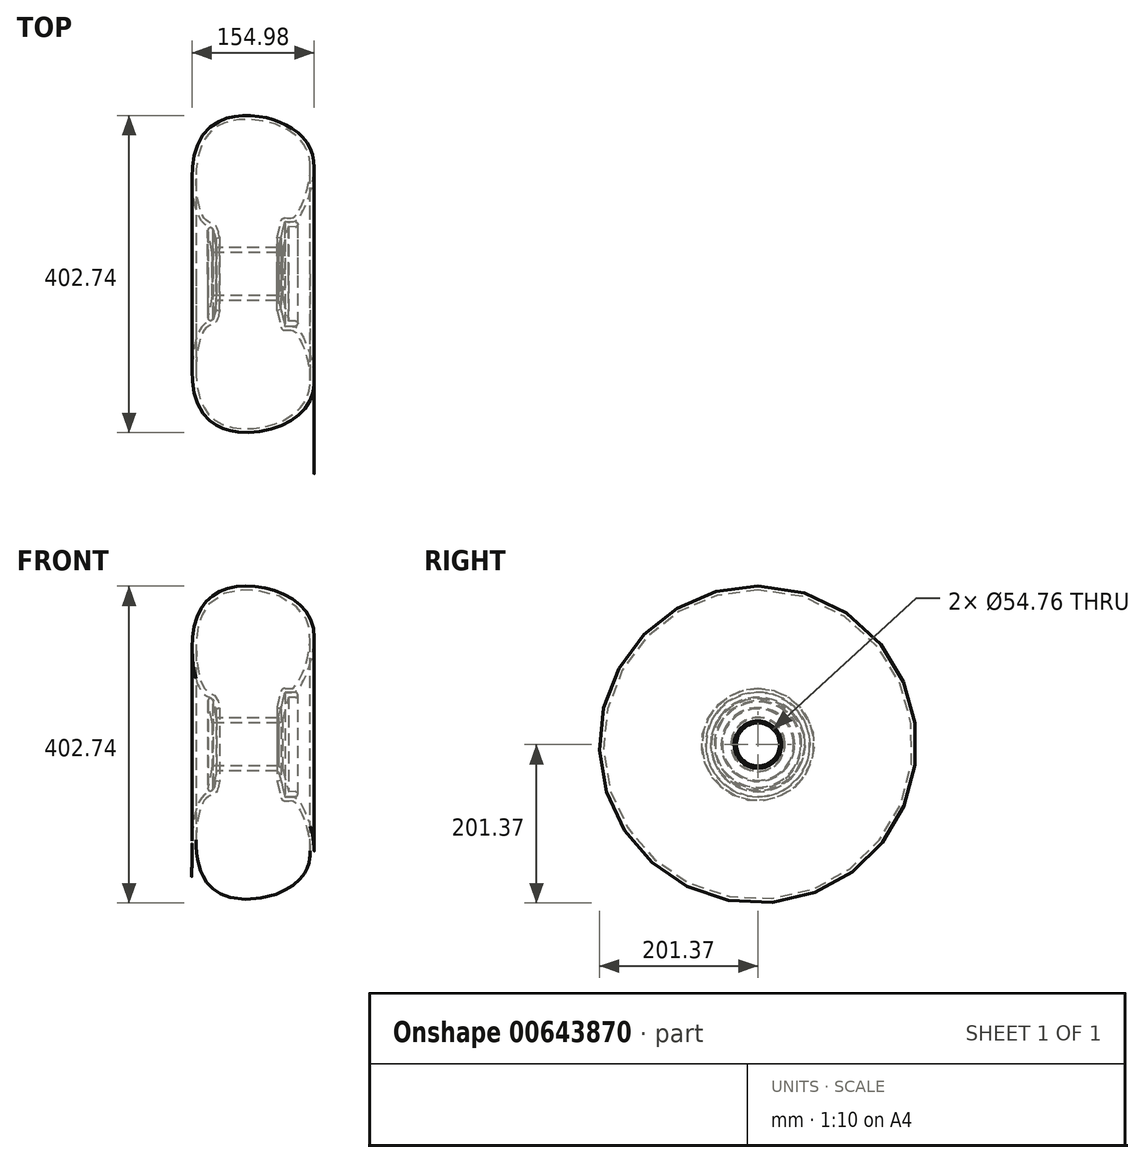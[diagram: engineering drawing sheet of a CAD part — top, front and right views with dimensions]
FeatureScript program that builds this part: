
annotation { "Feature Type Name" : "Feature", "Feature Type Description" : "" }
export const myFeature = defineFeature(function(context is Context, id is Id, definition is map)
    precondition{}
    {
        {
            var Q0;
            Q0=qCreatedBy(makeId("Front.planeOp"),FACE);
            var sketch = newSketch(context, id + "F0", { "sketchPlane" : qUnion([Q0])});
            skLineSegment(sketch, "E0", {"start": v(-28.23, 33.73) * mm, "end": v(49.08, 33.73) * mm});
            skLineSegment(sketch, "E1", {"start": v(50.61, 34.5) * mm, "end": v(49.08, 33.73) * mm});
            skLineSegment(sketch, "E2", {"start": v(49.08, 33.73) * mm, "end": v(50.61, 34.5) * mm});
            skLineSegment(sketch, "E3", {"start": v(58.9, 66.45) * mm, "end": v(50.61, 34.5) * mm});
            skLineSegment(sketch, "E4", {"start": v(72.2, 66.15) * mm, "end": v(58.9, 66.45) * mm});
            skLineSegment(sketch, "E5", {"start": v(-32.55, 55.46) * mm, "end": v(-28.23, 33.73) * mm});
            skLineSegment(sketch, "E6.0", {"start": v(72.05, 59.8) * mm, "end": v(63.79, 59.99) * mm});
            skLineSegment(sketch, "E6.1", {"start": v(-38.78, 54.22) * mm, "end": v(-33.44, 27.38) * mm});
            skLineSegment(sketch, "E6.2", {"start": v(-33.44, 27.38) * mm, "end": v(50.6, 27.38) * mm});
            skLineSegment(sketch, "E6.3", {"start": v(56.04, 30.14) * mm, "end": v(50.6, 27.38) * mm});
            skLineSegment(sketch, "E6.4", {"start": v(63.79, 59.99) * mm, "end": v(56.04, 30.14) * mm});
            skArc(sketch, "E7", {"start": v(72.05, 59.8) * mm, "mid": v(75.3, 62.9) * mm, "end": v(72.2, 66.15) * mm});
            skArc(sketch, "E8", {"start": v(-32.55, 55.46) * mm, "mid": v(-36.46, 58.82) * mm, "end": v(-38.78, 54.22) * mm});
            skLineSegment(sketch, "E9", {"start": v(0, 0) * mm, "end": v(20.87, 0) * mm, "construction": true});
            skSolve(sketch);
        }
        {
            var Q0;
            Q0 = qSketchRegion(id + "F0", true);
            var Q1;
            Q1=sQuery(id+"F0.wireOp",EDGE,"E9");
            revolve(context, id + "F1", {"entities" : qUnion([Q0]), "axis" : qUnion([Q1]), "revolveType" : RevolveType.FULL});
        }
        {
            var Q0;
            Q0=qCreatedBy(makeId("Front.planeOp"),FACE);
            var sketch = newSketch(context, id + "F2", { "sketchPlane" : qUnion([Q0])});
            skLineSegment(sketch, "E10", {"start": v(53.97, 45.4) * mm, "end": v(58.9, 66.45) * mm});
            skLineSegment(sketch, "E11", {"start": v(50.61, 34.5) * mm, "end": v(58.9, 66.45) * mm});
            skFitSpline(sketch, "E12", {"points": [v(58.9, 66.45) * mm, v(76.88, 71.82) * mm, v(93.15, 154.6) * mm, v(13.57, 201.31) * mm, v(-52.17, 164.12) * mm, v(-46.36, 66.45) * mm, v(-32.61, 57.36) * mm, v(-28.88, 45.27) * mm], "startDerivative": vector(355.83, -13.94) * mm, "endDerivative": vector(60.8, -192.56) * mm});
            skFitSpline(sketch, "E13.0", {"points": [v(59.1, 71.44) * mm, v(60.96, 71.37) * mm, v(63.36, 71.27) * mm, v(65.83, 71.25) * mm, v(67.31, 71.31) * mm, v(68.44, 71.45) * mm, v(69.25, 71.64) * mm, v(69.84, 71.86) * mm, v(70.36, 72.15) * mm, v(70.95, 72.6) * mm, v(71.7, 73.33) * mm, v(72.6, 74.42) * mm, v(73.65, 75.89) * mm, v(74.8, 77.68) * mm, v(76.44, 80.47) * mm, v(78.6, 84.62) * mm, v(81.23, 90.5) * mm, v(83.76, 97.08) * mm, v(86.1, 104.22) * mm, v(88.1, 111.74) * mm, v(89.66, 119.5) * mm, v(90.69, 127.34) * mm, v(91.07, 135.07) * mm, v(90.77, 141.3) * mm, v(90.12, 146.07) * mm, v(89.43, 149.52) * mm, v(88.66, 152.28) * mm, v(87.94, 154.4) * mm, v(86.73, 157.55) * mm, v(84.49, 162.04) * mm, v(80.63, 167.58) * mm, v(75.98, 172.69) * mm, v(68.83, 178.9) * mm, v(58.3, 185.47) * mm, v(43.91, 191.33) * mm, v(31.17, 194.46) * mm, v(20.96, 195.88) * mm, v(13.4, 196.4) * mm, v(6.04, 196.39) * mm, v(-3.4, 195.62) * mm, v(-14.44, 193.27) * mm, v(-26.12, 188.15) * mm, v(-34.36, 181.92) * mm, v(-39.98, 175.67) * mm, v(-43.07, 171.2) * mm, v(-45.27, 167.26) * mm, v(-46.78, 164.12) * mm, v(-48.14, 160.8) * mm, v(-49.36, 157.26) * mm, v(-50.43, 153.55) * mm, v(-51.67, 148.39) * mm, v(-52.87, 141.6) * mm, v(-53.75, 133.08) * mm, v(-54.23, 121.48) * mm, v(-53.72, 109.87) * mm, v(-52.37, 98.94) * mm, v(-50.96, 91.26) * mm, v(-49.22, 84.3) * mm, v(-47.54, 79.24) * mm, v(-46.09, 75.75) * mm, v(-44.97, 73.43) * mm, v(-43.83, 71.46) * mm, v(-42.9, 70.12) * mm, v(-42.19, 69.24) * mm, v(-41.48, 68.46) * mm, v(-40.58, 67.64) * mm, v(-39.5, 66.83) * mm, v(-38.36, 66.14) * mm, v(-37.18, 65.53) * mm, v(-35.93, 64.96) * mm, v(-34.6, 64.4) * mm, v(-33.2, 63.76) * mm, v(-31.95, 63.11) * mm, v(-30.91, 62.46) * mm, v(-30.12, 61.88) * mm, v(-29.34, 61.2) * mm, v(-28.59, 60.39) * mm, v(-27.95, 59.54) * mm, v(-27.24, 58.4) * mm, v(-26.57, 56.96) * mm, v(-26.02, 55.3) * mm, v(-25.62, 53.7) * mm, v(-25.31, 52.17) * mm, v(-25.03, 50.7) * mm, v(-24.67, 48.83) * mm, v(-24.36, 47.55) * mm, v(-24.12, 46.77) * mm]});
            skLineSegment(sketch, "E14.0", {"start": v(49.1, 46.55) * mm, "end": v(54.04, 67.59) * mm});
            skArc(sketch, "E15", {"start": v(59.1, 71.44) * mm, "mid": v(55.88, 70.43) * mm, "end": v(54.04, 67.59) * mm});
            skLineSegment(sketch, "E16", {"start": v(-28.88, 45.27) * mm, "end": v(-24.12, 46.77) * mm});
            skLineSegment(sketch, "E17", {"start": v(53.97, 45.4) * mm, "end": v(49.1, 46.55) * mm});
            skSolve(sketch);
        }
        {
            var Q0;
            Q0 = qSketchRegion(id + "F2", true);
            var Q1;
            Q1 = qSketchRegion(id + "F0", true);
            var Q2;
            Q2=sQuery(id+"F0.wireOp",EDGE,"E9");
            revolve(context, id + "F3", {"entities" : qUnion([Q0, Q1]), "axis" : qUnion([Q2]), "revolveType" : RevolveType.FULL, "surfaceOperationType" : NewSurfaceOperationType.NEW});
        }
    });
